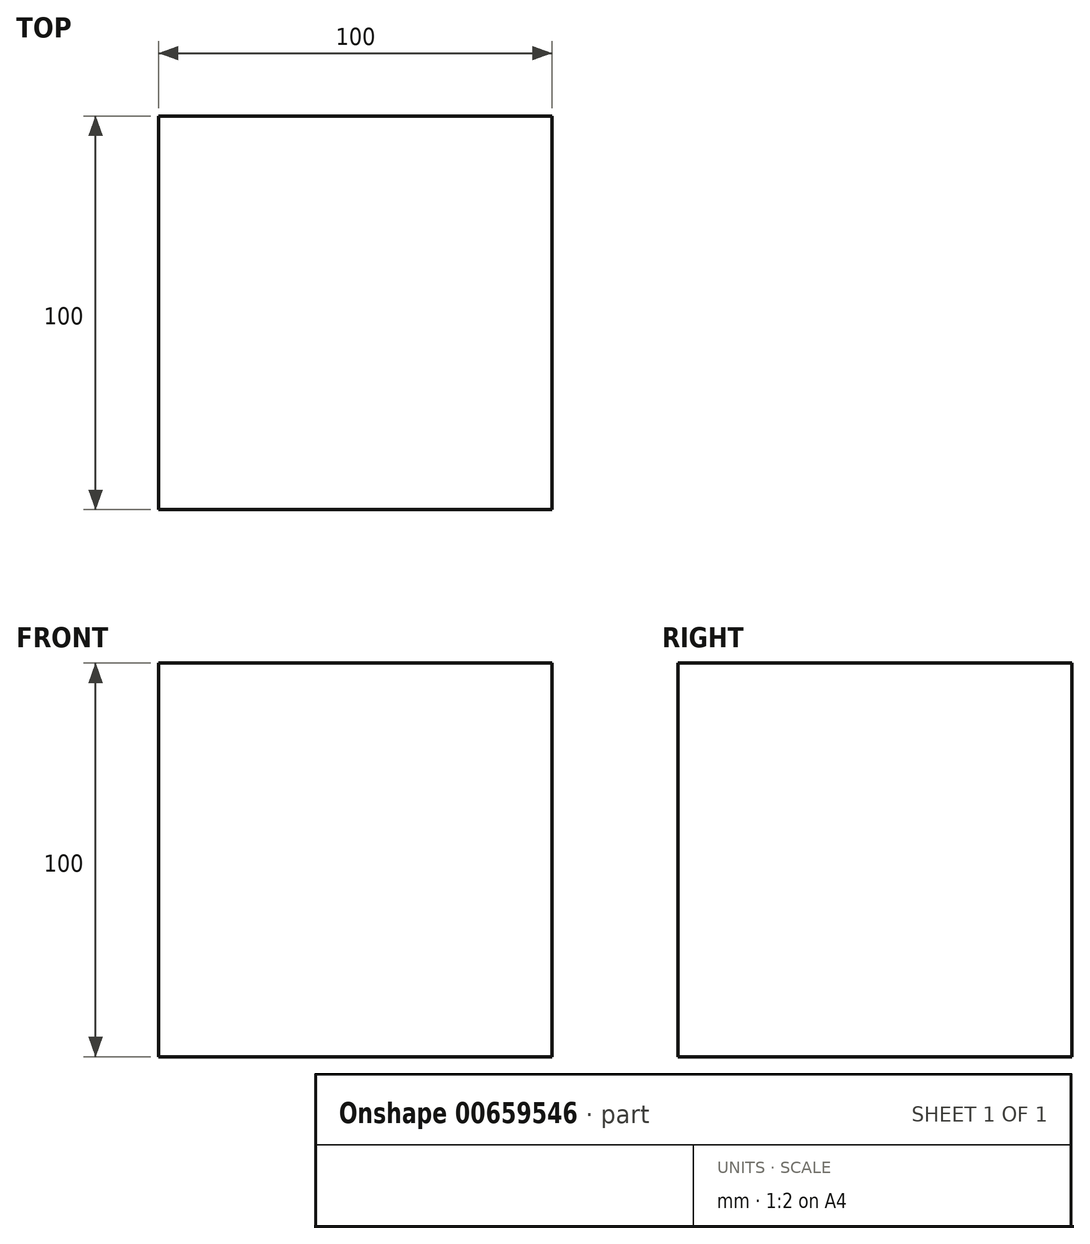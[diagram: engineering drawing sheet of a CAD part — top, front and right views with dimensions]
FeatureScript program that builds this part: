
annotation { "Feature Type Name" : "Feature", "Feature Type Description" : "" }
export const myFeature = defineFeature(function(context is Context, id is Id, definition is map)
    precondition{}
    {
        {
            var Q0;
            Q0=qCreatedBy(makeId("Top.planeOp"),FACE);
            var sketch = newSketch(context, id + "F0", { "sketchPlane" : qUnion([Q0])});
            skLineSegment(sketch, "E0.bottom", {"start": v(-50, 50) * mm, "end": v(50, 50) * mm});
            skLineSegment(sketch, "E0.top", {"start": v(-50, -50) * mm, "end": v(50, -50) * mm});
            skLineSegment(sketch, "E0.left", {"start": v(-50, 50) * mm, "end": v(-50, -50) * mm});
            skLineSegment(sketch, "E0.right", {"start": v(50, 50) * mm, "end": v(50, -50) * mm});
            skSolve(sketch);
        }
        {
            var Q0;
            Q0 = qSketchRegion(id + "F0", true);
            extrude(context, id + "F1", {"entities" : qUnion([Q0]), "endBound" : BoundingType.SYMMETRIC, "depth" : 100 * mm, "offsetDistance" : 25 * mm});
        }
    });
